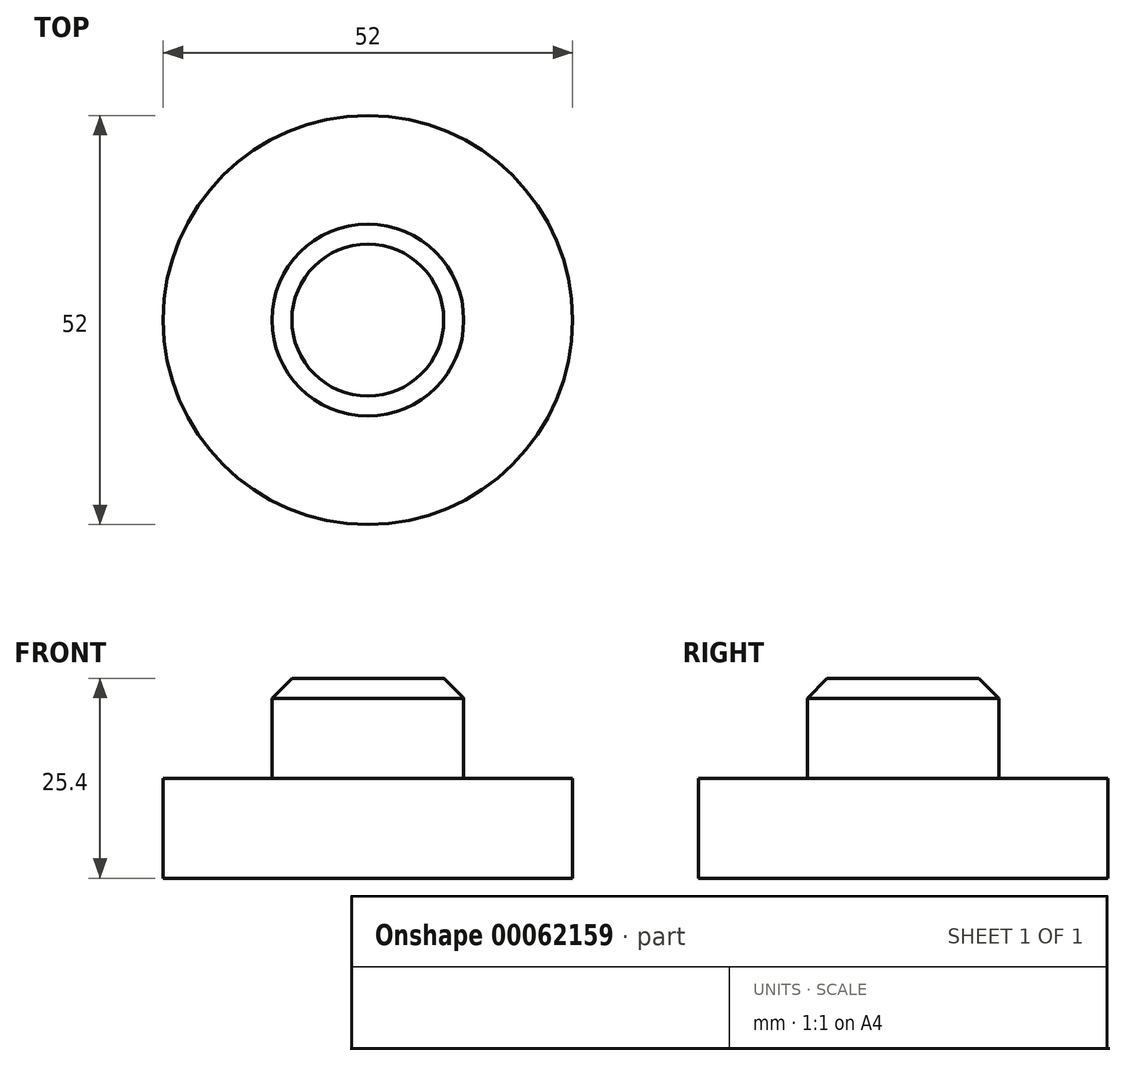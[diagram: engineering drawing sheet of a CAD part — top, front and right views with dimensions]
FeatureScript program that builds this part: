
annotation { "Feature Type Name" : "Feature", "Feature Type Description" : "" }
export const myFeature = defineFeature(function(context is Context, id is Id, definition is map)
    precondition{}
    {
        {
            var Q0;
            Q0=qCreatedBy(makeId("Top.planeOp"),FACE);
            var sketch = newSketch(context, id + "F0", { "sketchPlane" : qUnion([Q0])});
            skCircle(sketch, "E0", {"center": v(0, 0) * mm, "radius": 26 * mm});
            skSolve(sketch);
        }
        {
            var Q0;
            Q0=makeQuery(id+"F0.imprint","IMPRINT",FACE,{"disambiguationData":[TD([[makeQuery(id+"F0.imprint","IMPRINT",EDGE,{"derivedFrom":sQuery(id+"F0.wireOp",EDGE,"E0")}),1.0]])]});
            extrude(context, id + "F1", {"entities" : qUnion([Q0]), "oppositeDirection" : true, "depth" : 12.7 * mm});
        }
        {
            var Q0;
            Q0=makeQuery(id+"F1.opExtrude","CAP_FACE",FACE,{"disambiguationData":[OSD([sQuery(id+"F0.wireOp",EDGE,"E0")])],"isStart":true});
            var sketch = newSketch(context, id + "F2", { "sketchPlane" : qUnion([Q0])});
            skCircle(sketch, "E1", {"center": v(0, 0) * mm, "radius": 12.19 * mm});
            skSolve(sketch);
        }
        {
            var Q0;
            Q0=makeQuery(id+"F2.imprint","IMPRINT",FACE,{"disambiguationData":[TD([[makeQuery(id+"F2.imprint","IMPRINT",EDGE,{"derivedFrom":sQuery(id+"F2.wireOp",EDGE,"E1")}),1.0]])]});
            extrude(context, id + "F3", {"entities" : qUnion([Q0]), "operationType" : NewBodyOperationType.ADD, "depth" : 12.7 * mm});
        }
        {
            var Q0;
            Q0=makeQuery(id+"F3.opExtrude","CAP_EDGE",EDGE,{"disambiguationData":[OSD([sQuery(id+"F2.wireOp",EDGE,"E1")])],"isStart":false});
            chamfer(context, id + "F4", {"entities" : qUnion([Q0]), "width" : 2.54 * mm, "tangentPropagation" : true});
        }
    });
